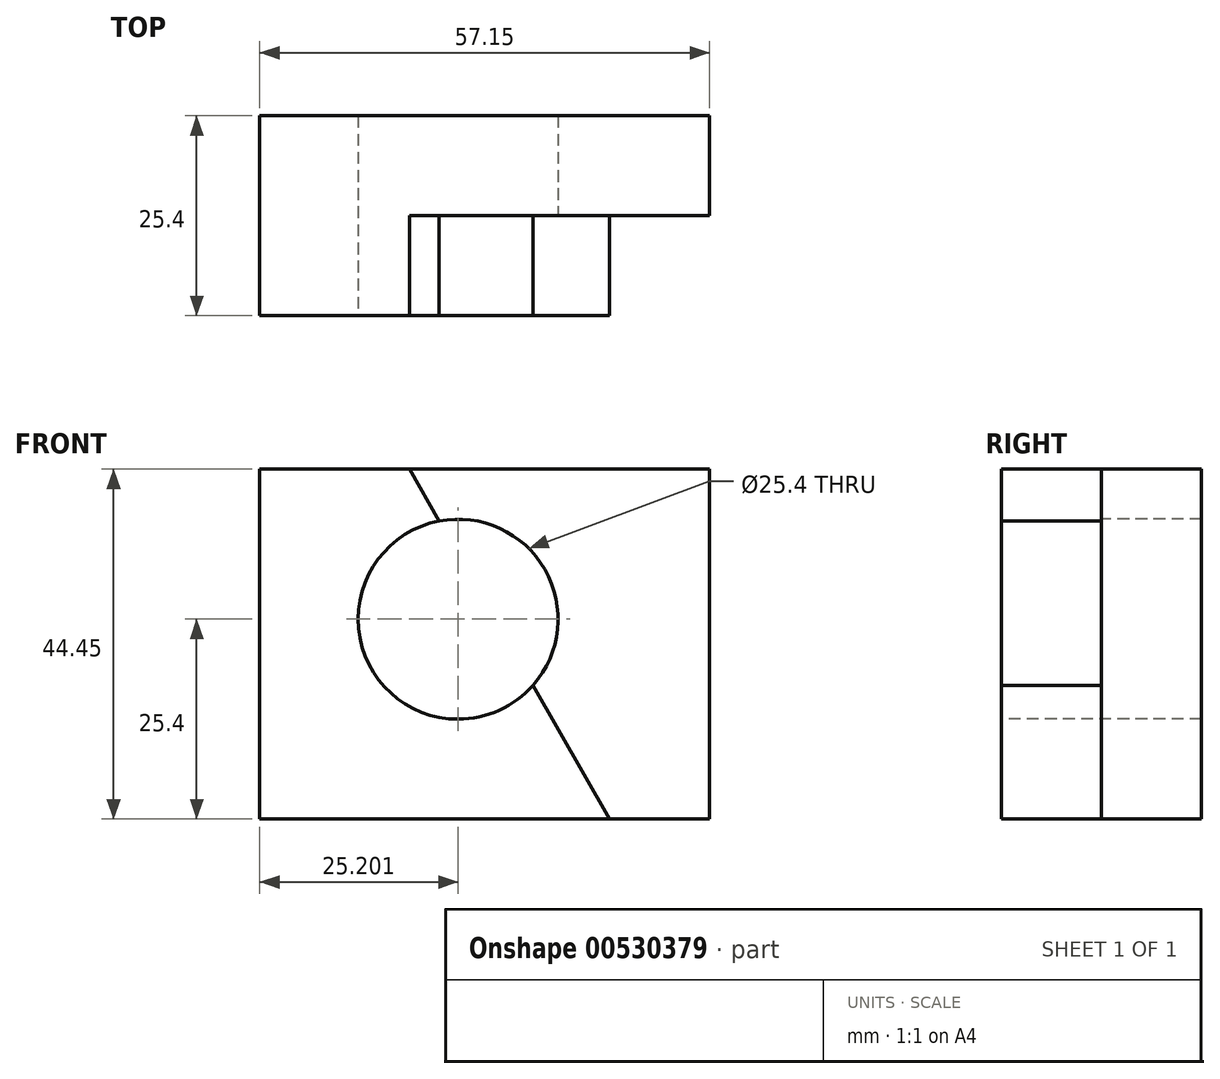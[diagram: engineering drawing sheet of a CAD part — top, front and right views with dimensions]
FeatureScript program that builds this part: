
annotation { "Feature Type Name" : "Feature", "Feature Type Description" : "" }
export const myFeature = defineFeature(function(context is Context, id is Id, definition is map)
    precondition{}
    {
        {
            var Q0;
            Q0=qCreatedBy(makeId("Front.planeOp"),FACE);
            var sketch = newSketch(context, id + "F0", { "sketchPlane" : qUnion([Q0])});
            skLineSegment(sketch, "E0", {"start": v(-57.15, 44.45) * mm, "end": v(-57.15, 0) * mm});
            skLineSegment(sketch, "E1", {"start": v(-57.15, 0) * mm, "end": v(0, 0) * mm});
            skLineSegment(sketch, "E2", {"start": v(0, 0) * mm, "end": v(0, 44.45) * mm});
            skLineSegment(sketch, "E3", {"start": v(0, 44.45) * mm, "end": v(-57.15, 44.45) * mm});
            skSolve(sketch);
        }
        {
            var Q0;
            Q0=makeQuery(id+"F0.imprint","IMPRINT",FACE,{"disambiguationData":[TD([[makeQuery(id+"F0.imprint","IMPRINT",EDGE,{"derivedFrom":sQuery(id+"F0.wireOp",EDGE,"E0")}),1.0]])]});
            extrude(context, id + "F1", {"entities" : qUnion([Q0]), "depth" : 25.4 * mm, "offsetDistance" : 25.4 * mm});
        }
        {
            var Q0;
            Q0=makeQuery(id+"F1.opExtrude","CAP_FACE",FACE,{"disambiguationData":[OSD([sQuery(id+"F0.wireOp",EDGE,"E0"),sQuery(id+"F0.wireOp",EDGE,"E1"),sQuery(id+"F0.wireOp",EDGE,"E2"),sQuery(id+"F0.wireOp",EDGE,"E3")])],"isStart":false});
            var sketch = newSketch(context, id + "F2", { "sketchPlane" : qUnion([Q0])});
            skLineSegment(sketch, "E4", {"start": v(-38.1, 44.45) * mm, "end": v(-12.7, 0) * mm});
            skLineSegment(sketch, "E5", {"start": v(-12.7, 0) * mm, "end": v(0, 0) * mm});
            skLineSegment(sketch, "E6", {"start": v(0, 0) * mm, "end": v(0, 44.45) * mm});
            skLineSegment(sketch, "E7", {"start": v(0, 44.45) * mm, "end": v(-38.1, 44.45) * mm});
            skSolve(sketch);
        }
        {
            var Q0;
            Q0=makeQuery(id+"F2.imprint","IMPRINT",FACE,{"disambiguationData":[TD([[makeQuery(id+"F2.imprint","IMPRINT",EDGE,{"derivedFrom":sQuery(id+"F2.wireOp",EDGE,"E4")}),1.0]])]});
            extrude(context, id + "F3", {"entities" : qUnion([Q0]), "operationType" : NewBodyOperationType.REMOVE, "oppositeDirection" : true, "depth" : 12.7 * mm, "offsetDistance" : 25.4 * mm});
        }
        {
            var Q0;
            Q0=makeQuery(id+"F1.opExtrude","CAP_FACE",FACE,{"disambiguationData":[OSD([sQuery(id+"F0.wireOp",EDGE,"E0"),sQuery(id+"F0.wireOp",EDGE,"E1"),sQuery(id+"F0.wireOp",EDGE,"E2"),sQuery(id+"F0.wireOp",EDGE,"E3")])],"isStart":false});
            var sketch = newSketch(context, id + "F4", { "sketchPlane" : qUnion([Q0])});
            skCircle(sketch, "E8", {"center": v(-31.95, 25.4) * mm, "radius": 12.7 * mm});
            skSolve(sketch);
        }
        {
            var Q0;
            {var subQ0=sQuery(id+"F4.wireOp",EDGE,"E8");var subQ1=makeQuery(id+"F3.boolean.opBoolean","COPY",EDGE,{"derivedFrom":makeQuery(id+"F3.opExtrude","CAP_EDGE",EDGE,{"disambiguationData":[OSD([sQuery(id+"F2.wireOp",EDGE,"E4")])],"isStart":true})});var subQ2=makeQuery(id+"F4.imprint","INTERSECT",VERTEX,{"disambiguationData":[OD(0.0)],"derivedFrom":[subQ1,subQ0]});Q0=makeQuery(id+"F4.imprint","IMPRINT",FACE,{"disambiguationData":[TD([[makeQuery(id+"F4.imprint","IMPRINT",EDGE,{"disambiguationData":[TD([[subQ2,1.0]])],"derivedFrom":subQ0}),1.0]])]});}
            var Q1;
            {var subQ0=sQuery(id+"F4.wireOp",EDGE,"E8");var subQ1=makeQuery(id+"F3.boolean.opBoolean","COPY",EDGE,{"derivedFrom":makeQuery(id+"F3.opExtrude","CAP_EDGE",EDGE,{"disambiguationData":[OSD([sQuery(id+"F2.wireOp",EDGE,"E4")])],"isStart":true})});var subQ2=makeQuery(id+"F4.imprint","INTERSECT",VERTEX,{"disambiguationData":[OD(0.0)],"derivedFrom":[subQ1,subQ0]});Q1=makeQuery(id+"F4.imprint","IMPRINT",FACE,{"disambiguationData":[TD([[makeQuery(id+"F4.imprint","IMPRINT",EDGE,{"disambiguationData":[TD([[subQ2,-1.0]])],"derivedFrom":subQ0}),1.0]])]});}
            extrude(context, id + "F5", {"entities" : qUnion([Q0, Q1]), "operationType" : NewBodyOperationType.REMOVE, "oppositeDirection" : true, "depth" : 25.4 * mm, "offsetDistance" : 25.4 * mm});
        }
    });
